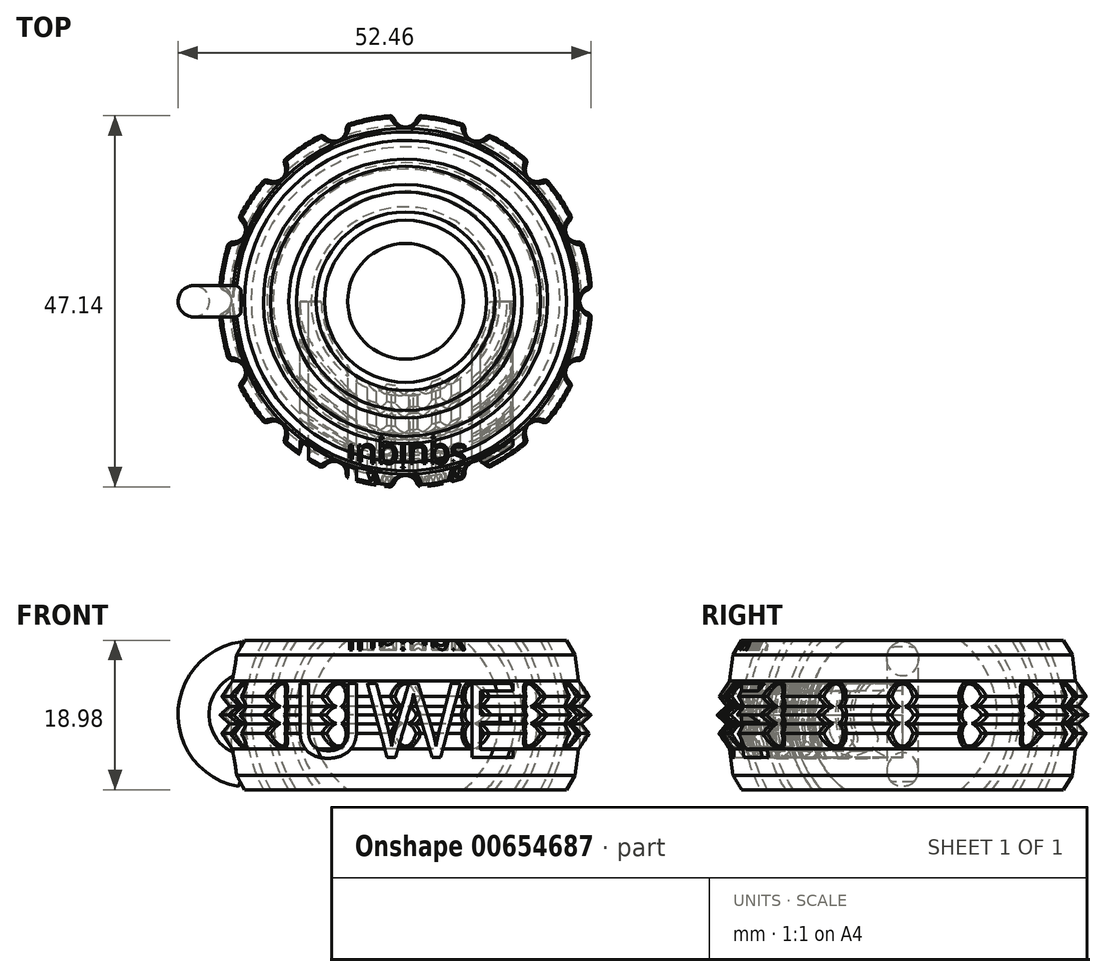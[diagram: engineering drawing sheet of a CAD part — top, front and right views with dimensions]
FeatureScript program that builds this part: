
annotation { "Feature Type Name" : "Feature", "Feature Type Description" : "" }
export const myFeature = defineFeature(function(context is Context, id is Id, definition is map)
    precondition{}
    {
        {
            var Q0;
            Q0=qCreatedBy(makeId("Top.planeOp"),FACE);
            var sketch = newSketch(context, id + "F0", { "sketchPlane" : qUnion([Q0])});
            skArc(sketch, "E0", {"start": v(0, 12) * mm, "mid": v(-12, 0) * mm, "end": v(0, -12) * mm});
            skLineSegment(sketch, "E1", {"start": v(0, 12) * mm, "end": v(0, -12) * mm});
            skArc(sketch, "E2.0", {"start": v(0, 14) * mm, "mid": v(-14, 0) * mm, "end": v(0, -14) * mm});
            skLineSegment(sketch, "E3", {"start": v(0, 14) * mm, "end": v(0, 12) * mm});
            skLineSegment(sketch, "E4", {"start": v(0, -12) * mm, "end": v(0, -14) * mm});
            skSolve(sketch);
        }
        {
            var Q0;
            Q0=makeQuery(id+"F0.imprint","IMPRINT",FACE,{"disambiguationData":[TD([[makeQuery(id+"F0.imprint","IMPRINT",EDGE,{"derivedFrom":sQuery(id+"F0.wireOp",EDGE,"E0")}),-1.0]])]});
            var Q1;
            Q1=sQuery(id+"F0.wireOp",EDGE,"E1");
            revolve(context, id + "F1", {"entities" : qUnion([Q0]), "axis" : qUnion([Q1]), "revolveType" : RevolveType.FULL});
        }
        {
            var Q0;
            Q0=qCreatedBy(makeId("Top.planeOp"),FACE);
            var sketch = newSketch(context, id + "F2", { "sketchPlane" : qUnion([Q0])});
            skLineSegment(sketch, "E5.bottom", {"start": v(37.77, 9.49) * mm, "end": v(-37.77, 9.49) * mm});
            skLineSegment(sketch, "E5.top", {"start": v(37.77, 45.25) * mm, "end": v(-37.77, 45.25) * mm});
            skLineSegment(sketch, "E5.left", {"start": v(37.77, 9.49) * mm, "end": v(37.77, 45.25) * mm});
            skLineSegment(sketch, "E5.right", {"start": v(-37.77, 9.49) * mm, "end": v(-37.77, 45.25) * mm});
            skPoint(sketch, "E5.middle", {"position": v(0, 27.37) * mm});
            skLineSegment(sketch, "E6.MirrorCS", {"start": v(-37.77, -9.49) * mm, "end": v(-37.77, -45.25) * mm});
            skLineSegment(sketch, "E7.MirrorCS", {"start": v(37.77, -9.49) * mm, "end": v(37.77, -45.25) * mm});
            skLineSegment(sketch, "E8.MirrorCS", {"start": v(37.77, -45.25) * mm, "end": v(-37.77, -45.25) * mm});
            skLineSegment(sketch, "E9.MirrorCS", {"start": v(37.77, -9.49) * mm, "end": v(-37.77, -9.49) * mm});
            skPoint(sketch, "E10.MirrorP", {"position": v(0, -27.37) * mm});
            skSolve(sketch);
        }
        {
            var Q0;
            Q0=qCreatedBy(makeId("Top.planeOp"),FACE);
            var sketch = newSketch(context, id + "F3", { "sketchPlane" : qUnion([Q0])});
            skArc(sketch, "E11.0", {"start": v(0, 14.8) * mm, "mid": v(-14.8, 0) * mm, "end": v(0, -14.8) * mm});
            skArc(sketch, "E12.0", {"start": v(0, 16.8) * mm, "mid": v(-16.8, 0) * mm, "end": v(0, -16.8) * mm});
            skLineSegment(sketch, "E13", {"start": v(0, -14.8) * mm, "end": v(0, -16.8) * mm});
            skLineSegment(sketch, "E14", {"start": v(0, 14.8) * mm, "end": v(0, 16.8) * mm});
            skSolve(sketch);
        }
        {
            var Q0;
            Q0=makeQuery(id+"F3.imprint","IMPRINT",FACE,{"disambiguationData":[TD([[makeQuery(id+"F3.imprint","IMPRINT",EDGE,{"derivedFrom":sQuery(id+"F3.wireOp",EDGE,"E11.0")}),-1.0]])]});
            var Q1;
            Q1=sQuery(id+"F0.wireOp",EDGE,"E1");
            revolve(context, id + "F4", {"entities" : qUnion([Q0]), "axis" : qUnion([Q1]), "revolveType" : RevolveType.FULL});
        }
        {
            var Q0;
            Q0=qCreatedBy(makeId("Top.planeOp"),FACE);
            var sketch = newSketch(context, id + "F5", { "sketchPlane" : qUnion([Q0])});
            skArc(sketch, "E15.0", {"start": v(0, 17.6) * mm, "mid": v(-17.6, 0) * mm, "end": v(0, -17.6) * mm});
            skArc(sketch, "E16.0", {"start": v(0, 19.6) * mm, "mid": v(-19.6, 0) * mm, "end": v(0, -19.6) * mm});
            skLineSegment(sketch, "E17", {"start": v(0, -17.6) * mm, "end": v(0, -19.6) * mm});
            skLineSegment(sketch, "E18", {"start": v(0, 17.6) * mm, "end": v(0, 19.6) * mm});
            skSolve(sketch);
        }
        {
            var Q0;
            Q0=qCreatedBy(makeId("Top.planeOp"),FACE);
            var sketch = newSketch(context, id + "F6", { "sketchPlane" : qUnion([Q0])});
            skArc(sketch, "E19.0", {"start": v(0, 20.4) * mm, "mid": v(-20.4, 0) * mm, "end": v(0, -20.4) * mm});
            skArc(sketch, "E20.0", {"start": v(0, 22.4) * mm, "mid": v(-6.34, 21.48) * mm, "end": v(-12.16, 18.81) * mm});
            skLineSegment(sketch, "E21", {"start": v(0, -20.4) * mm, "end": v(0, -22.4) * mm});
            skLineSegment(sketch, "E22", {"start": v(0, 20.4) * mm, "end": v(0, 22.4) * mm});
            skLineSegment(sketch, "E23", {"start": v(-12.16, 18.81) * mm, "end": v(-15.27, 18.35) * mm});
            skLineSegment(sketch, "E24", {"start": v(-15.27, 18.35) * mm, "end": v(-15.27, 16.39) * mm});
            skLineSegment(sketch, "E25", {"start": v(-15.27, 16.39) * mm, "end": v(-19.46, 13.16) * mm});
            skLineSegment(sketch, "E26", {"start": v(-19.46, 13.16) * mm, "end": v(-19.3, 11.37) * mm});
            skLineSegment(sketch, "E27", {"start": v(-19.3, 11.37) * mm, "end": v(-21.55, 7.65) * mm});
            skLineSegment(sketch, "E28", {"start": v(-21.55, 7.65) * mm, "end": v(-21.98, 4.32) * mm});
            skLineSegment(sketch, "E29", {"start": v(-21.98, 4.32) * mm, "end": v(-23.4, 2.34) * mm});
            skLineSegment(sketch, "E30", {"start": v(-23.4, 2.34) * mm, "end": v(-22.37, 1.12) * mm});
            skLineSegment(sketch, "E31", {"start": v(-22.37, 1.12) * mm, "end": v(-23.66, 0) * mm});
            skArc(sketch, "E32.trimOffspring", {"start": v(-12.16, -18.81) * mm, "mid": v(-6.34, -21.48) * mm, "end": v(0, -22.4) * mm});
            skLineSegment(sketch, "E33.MirrorCS", {"start": v(-23.4, -2.34) * mm, "end": v(-22.37, -1.12) * mm});
            skLineSegment(sketch, "E34.MirrorCS", {"start": v(-23.66, 0) * mm, "end": v(-22.4, 0) * mm});
            skLineSegment(sketch, "E35.MirrorCS", {"start": v(-21.98, -4.32) * mm, "end": v(-23.4, -2.34) * mm});
            skLineSegment(sketch, "E36.MirrorCS", {"start": v(-19.46, -13.16) * mm, "end": v(-19.3, -11.37) * mm});
            skLineSegment(sketch, "E37.MirrorCS", {"start": v(-15.27, -18.35) * mm, "end": v(-15.27, -16.39) * mm});
            skLineSegment(sketch, "E38.MirrorCS", {"start": v(-22.37, -1.12) * mm, "end": v(-23.66, 0) * mm});
            skLineSegment(sketch, "E39.MirrorCS", {"start": v(-19.3, -11.37) * mm, "end": v(-21.55, -7.65) * mm});
            skLineSegment(sketch, "E40.MirrorCS", {"start": v(-21.55, -7.65) * mm, "end": v(-21.98, -4.32) * mm});
            skLineSegment(sketch, "E41.MirrorCS", {"start": v(-12.16, -18.81) * mm, "end": v(-15.27, -18.35) * mm});
            skLineSegment(sketch, "E42.MirrorCS", {"start": v(-15.27, -16.39) * mm, "end": v(-19.46, -13.16) * mm});
            skPoint(sketch, "E43.end.orphan", {"position": v(-22.4, 0) * mm});
            skSolve(sketch);
        }
        {
            var Q0;
            Q0=makeQuery(id+"F5.imprint","IMPRINT",FACE,{"disambiguationData":[TD([[makeQuery(id+"F5.imprint","IMPRINT",EDGE,{"derivedFrom":sQuery(id+"F5.wireOp",EDGE,"E15.0")}),-1.0]])]});
            var Q1;
            Q1=sQuery(id+"F0.wireOp",EDGE,"E1");
            revolve(context, id + "F7", {"entities" : qUnion([Q0]), "axis" : qUnion([Q1]), "revolveType" : RevolveType.FULL});
        }
        {
            var Q0;
            Q0=makeQuery(id+"F6.imprint","IMPRINT",FACE,{"disambiguationData":[TD([[makeQuery(id+"F6.imprint","IMPRINT",EDGE,{"derivedFrom":sQuery(id+"F6.wireOp",EDGE,"E19.0")}),-1.0]])]});
            var Q1;
            Q1=sQuery(id+"F0.wireOp",EDGE,"E1");
            revolve(context, id + "F8", {"entities" : qUnion([Q0]), "axis" : qUnion([Q1]), "revolveType" : RevolveType.FULL});
        }
        {
            var Q0;
            Q0 = qSketchRegion(id + "F2", true);
            extrude(context, id + "F9", {"entities" : qUnion([Q0]), "operationType" : NewBodyOperationType.REMOVE, "endBound" : BoundingType.SYMMETRIC, "oppositeDirection" : true, "depth" : 114 * mm, "offsetDistance" : 25 * mm});
        }
        {
            var Q0;
            Q0=qCreatedBy(makeId("Right.planeOp"),FACE);
            cPlane(context, id + "F10", {"entities" : qUnion([Q0]), "cplaneType" : CPlaneType.OFFSET, "offset" : 20.9 * mm, "oppositeDirection" : true, "width" : 150 * mm, "height" : 150 * mm});
        }
        {
            var Q0;
            Q0=qCreatedBy(makeId("Top.planeOp"),FACE);
            var sketch = newSketch(context, id + "F11", { "sketchPlane" : qUnion([Q0])});
            skArc(sketch, "E44", {"start": v(-20.93, 8.53) * mm, "mid": v(-28.13, 0.1) * mm, "end": v(-20.96, -8.37) * mm});
            skSolve(sketch);
        }
        {
            var Q0;
            Q0=qCreatedBy(id+"F10.planeOp",FACE);
            var sketch = newSketch(context, id + "F12", { "sketchPlane" : qUnion([Q0])});
            skCircle(sketch, "E45", {"center": v(7.3, 0) * mm, "radius": 2 * mm});
            skSolve(sketch);
        }
        {
            var Q0;
            Q0=qCreatedBy(makeId("Front.planeOp"),FACE);
            var sketch = newSketch(context, id + "F13", { "sketchPlane" : qUnion([Q0])});
            skCircle(sketch, "E46", {"center": v(23.63, 0) * mm, "radius": 1.5 * mm});
            skCircle(sketch, "E47.1.0", {"center": v(21.83, 9.04) * mm, "radius": 1.5 * mm});
            skCircle(sketch, "E47.2.0", {"center": v(16.7, 16.7) * mm, "radius": 1.5 * mm});
            skCircle(sketch, "E47.3.0", {"center": v(9.04, 21.83) * mm, "radius": 1.5 * mm});
            skCircle(sketch, "E47.4.0", {"center": v(0, 23.63) * mm, "radius": 1.5 * mm});
            skCircle(sketch, "E47.5.0", {"center": v(-9.04, 21.83) * mm, "radius": 1.5 * mm});
            skCircle(sketch, "E47.6.0", {"center": v(-16.7, 16.7) * mm, "radius": 1.5 * mm});
            skCircle(sketch, "E47.7.0", {"center": v(-21.83, 9.04) * mm, "radius": 1.5 * mm});
            skCircle(sketch, "E47.8.0", {"center": v(-23.63, 0) * mm, "radius": 1.5 * mm});
            skCircle(sketch, "E47.9.0", {"center": v(-21.83, -9.04) * mm, "radius": 1.5 * mm});
            skCircle(sketch, "E47.10.0", {"center": v(-16.7, -16.7) * mm, "radius": 1.5 * mm});
            skCircle(sketch, "E47.11.0", {"center": v(-9.04, -21.83) * mm, "radius": 1.5 * mm});
            skCircle(sketch, "E47.12.0", {"center": v(0, -23.63) * mm, "radius": 1.5 * mm});
            skCircle(sketch, "E47.13.0", {"center": v(9.04, -21.83) * mm, "radius": 1.5 * mm});
            skCircle(sketch, "E47.14.0", {"center": v(16.7, -16.7) * mm, "radius": 1.5 * mm});
            skCircle(sketch, "E47.15.0", {"center": v(21.83, -9.04) * mm, "radius": 1.5 * mm});
            skPoint(sketch, "E47.center", {"position": v(0, 0) * mm});
            skSolve(sketch);
        }
        {
            var Q0;
            Q0 = qSketchRegion(id + "F13", true);
            extrude(context, id + "F14", {"entities" : qUnion([Q0]), "operationType" : NewBodyOperationType.REMOVE, "endBound" : BoundingType.SYMMETRIC, "oppositeDirection" : true, "depth" : 25 * mm, "offsetDistance" : 25 * mm});
        }
        {
            var Q0;
            Q0=makeQuery(id+"F12.imprint","IMPRINT",FACE,{"disambiguationData":[TD([[makeQuery(id+"F12.imprint","IMPRINT",EDGE,{"derivedFrom":sQuery(id+"F12.wireOp",EDGE,"E45")}),1.0]])]});
            var Q1;
            Q1=sQuery(id+"F11.wireOp",EDGE,"E44");
            sweep(context, id + "F15", {"operationType" : NewBodyOperationType.ADD, "profiles" : qUnion([Q0]), "path" : qUnion([Q1])});
        }
        {
            var Q0;
            Q0=makeQuery(id+"F14.boolean.opBoolean","COPY",FACE,{"derivedFrom":makeQuery(id+"F14.opExtrude","SWEPT_FACE",FACE,{"disambiguationData":[OSD([sQuery(id+"F13.wireOp",EDGE,"E46")])]})});
            var Q1;
            Q1=makeQuery(id+"F14.boolean.opBoolean","COPY",FACE,{"derivedFrom":makeQuery(id+"F14.opExtrude","SWEPT_FACE",FACE,{"disambiguationData":[OSD([sQuery(id+"F13.wireOp",EDGE,"E47.1.0")])]})});
            var Q2;
            Q2=makeQuery(id+"F14.boolean.opBoolean","COPY",FACE,{"derivedFrom":makeQuery(id+"F14.opExtrude","SWEPT_FACE",FACE,{"disambiguationData":[OSD([sQuery(id+"F13.wireOp",EDGE,"E47.2.0")])]})});
            var Q3;
            Q3=makeQuery(id+"F14.boolean.opBoolean","COPY",FACE,{"derivedFrom":makeQuery(id+"F14.opExtrude","SWEPT_FACE",FACE,{"disambiguationData":[OSD([sQuery(id+"F13.wireOp",EDGE,"E47.15.0")])]})});
            var Q4;
            Q4=makeQuery(id+"F14.boolean.opBoolean","COPY",FACE,{"derivedFrom":makeQuery(id+"F14.opExtrude","SWEPT_FACE",FACE,{"disambiguationData":[OSD([sQuery(id+"F13.wireOp",EDGE,"E47.14.0")])]})});
            var Q5;
            Q5=makeQuery(id+"F14.boolean.opBoolean","COPY",FACE,{"derivedFrom":makeQuery(id+"F14.opExtrude","SWEPT_FACE",FACE,{"disambiguationData":[OSD([sQuery(id+"F13.wireOp",EDGE,"E47.13.0")])]})});
            var Q6;
            Q6=makeQuery(id+"F14.boolean.opBoolean","COPY",FACE,{"derivedFrom":makeQuery(id+"F14.opExtrude","SWEPT_FACE",FACE,{"disambiguationData":[OSD([sQuery(id+"F13.wireOp",EDGE,"E47.12.0")])]})});
            var Q7;
            Q7=makeQuery(id+"F14.boolean.opBoolean","INTERSECT",EDGE,{"disambiguationData":[OD(0.0)],"derivedFrom":[makeQuery(id+"F8.opRevolve","SWEPT_FACE",FACE,{"disambiguationData":[OSD([sQuery(id+"F6.wireOp",EDGE,"E38.MirrorCS")])]}),makeQuery(id+"F14.opExtrude","SWEPT_FACE",FACE,{"disambiguationData":[OSD([sQuery(id+"F13.wireOp",EDGE,"E47.11.0")])]})]});
            var Q8;
            Q8=makeQuery(id+"F14.boolean.opBoolean","COPY",FACE,{"derivedFrom":makeQuery(id+"F14.opExtrude","SWEPT_FACE",FACE,{"disambiguationData":[OSD([sQuery(id+"F13.wireOp",EDGE,"E47.11.0")])]})});
            var Q9;
            Q9=makeQuery(id+"F14.boolean.opBoolean","COPY",FACE,{"derivedFrom":makeQuery(id+"F14.opExtrude","SWEPT_FACE",FACE,{"disambiguationData":[OSD([sQuery(id+"F13.wireOp",EDGE,"E47.10.0")])]})});
            var Q10;
            Q10=makeQuery(id+"F14.boolean.opBoolean","COPY",FACE,{"derivedFrom":makeQuery(id+"F14.opExtrude","SWEPT_FACE",FACE,{"disambiguationData":[OSD([sQuery(id+"F13.wireOp",EDGE,"E47.9.0")])]})});
            var Q11;
            Q11=makeQuery(id+"F14.boolean.opBoolean","COPY",FACE,{"disambiguationData":[TD([makeQuery(id+"F8.opRevolve","SWEPT_FACE",FACE,{"disambiguationData":[OSD([sQuery(id+"F6.wireOp",EDGE,"E29")])]})])],"derivedFrom":makeQuery(id+"F14.opExtrude","SWEPT_FACE",FACE,{"disambiguationData":[OSD([sQuery(id+"F13.wireOp",EDGE,"E47.8.0")])]})});
            var Q12;
            Q12=makeQuery(id+"F14.boolean.opBoolean","COPY",FACE,{"derivedFrom":makeQuery(id+"F14.opExtrude","SWEPT_FACE",FACE,{"disambiguationData":[OSD([sQuery(id+"F13.wireOp",EDGE,"E47.7.0")])]})});
            var Q13;
            Q13=makeQuery(id+"F14.boolean.opBoolean","COPY",FACE,{"derivedFrom":makeQuery(id+"F14.opExtrude","SWEPT_FACE",FACE,{"disambiguationData":[OSD([sQuery(id+"F13.wireOp",EDGE,"E47.6.0")])]})});
            var Q14;
            Q14=makeQuery(id+"F14.boolean.opBoolean","COPY",FACE,{"derivedFrom":makeQuery(id+"F14.opExtrude","SWEPT_FACE",FACE,{"disambiguationData":[OSD([sQuery(id+"F13.wireOp",EDGE,"E47.5.0")])]})});
            var Q15;
            Q15=makeQuery(id+"F14.boolean.opBoolean","COPY",FACE,{"derivedFrom":makeQuery(id+"F14.opExtrude","SWEPT_FACE",FACE,{"disambiguationData":[OSD([sQuery(id+"F13.wireOp",EDGE,"E47.4.0")])]})});
            var Q16;
            Q16=makeQuery(id+"F14.boolean.opBoolean","COPY",FACE,{"derivedFrom":makeQuery(id+"F14.opExtrude","SWEPT_FACE",FACE,{"disambiguationData":[OSD([sQuery(id+"F13.wireOp",EDGE,"E47.3.0")])]})});
            fillet(context, id + "F16", {"entities" : qUnion([Q0, Q1, Q2, Q3, Q4, Q5, Q6, Q7, Q8, Q9, Q10, Q11, Q12, Q13, Q14, Q15, Q16]), "radius" : 0.5 * mm, "tangentPropagation" : true, "allowEdgeOverflow" : false});
        }
        {
            var Q0;
            Q0=makeQuery(id+"F9.boolean.opBoolean","COPY",FACE,{"disambiguationData":[TD([makeQuery(id+"F1.opRevolve","SWEPT_FACE",FACE,{"disambiguationData":[OSD([sQuery(id+"F0.wireOp",EDGE,"E0")])]})])],"derivedFrom":makeQuery(id+"F9.opExtrude","SWEPT_FACE",FACE,{"disambiguationData":[OSD([sQuery(id+"F2.wireOp",EDGE,"E5.bottom")])]})});
            var sketch = newSketch(context, id + "F17", { "sketchPlane" : qUnion([Q0])});
            skText(sketch, "E48", { "text": "squiqui", "fontName": "OpenSans-Regular.ttf"});
            const initialGuessF17  = {"E48": [-0.0078, 0.01824, 1, 0, 0.0032]};
            skSetInitialGuess(sketch, initialGuessF17);
            skSolve(sketch);
        }
        {
            var Q0;
            Q0 = qSketchRegion(id + "F17", true);
            extrude(context, id + "F18", {"entities" : qUnion([Q0]), "operationType" : NewBodyOperationType.REMOVE, "oppositeDirection" : true, "depth" : 1.2 * mm, "offsetDistance" : 25 * mm});
        }
        {
            var Q0;
            Q0=qCreatedBy(makeId("Top.planeOp"),FACE);
            var sketch = newSketch(context, id + "F19", { "sketchPlane" : qUnion([Q0])});
            skLineSegment(sketch, "E49", {"start": v(33.61, 0) * mm, "end": v(-41.39, 0) * mm});
            skSolve(sketch);
        }
        {
            var Q0;
            Q0=makeQuery(id+"F1.opRevolve","SWEPT_BODY",BODY,{"disambiguationData":[OSD([sQuery(id+"F0.wireOp",EDGE,"E0"),sQuery(id+"F0.wireOp",EDGE,"E2.0"),sQuery(id+"F0.wireOp",EDGE,"E3"),sQuery(id+"F0.wireOp",EDGE,"E4")])]});
            var Q1;
            Q1=makeQuery(id+"F4.opRevolve","SWEPT_BODY",BODY,{"disambiguationData":[OSD([sQuery(id+"F3.wireOp",EDGE,"E11.0"),sQuery(id+"F3.wireOp",EDGE,"E12.0"),sQuery(id+"F3.wireOp",EDGE,"E13"),sQuery(id+"F3.wireOp",EDGE,"E14")])]});
            var Q2;
            Q2=makeQuery(id+"F8.opRevolve","SWEPT_BODY",BODY,{"disambiguationData":[OSD([sQuery(id+"F6.wireOp",EDGE,"E19.0"),sQuery(id+"F6.wireOp",EDGE,"E20.0"),sQuery(id+"F6.wireOp",EDGE,"E21"),sQuery(id+"F6.wireOp",EDGE,"E22"),sQuery(id+"F6.wireOp",EDGE,"E23"),sQuery(id+"F6.wireOp",EDGE,"E24"),sQuery(id+"F6.wireOp",EDGE,"E25"),sQuery(id+"F6.wireOp",EDGE,"E26"),sQuery(id+"F6.wireOp",EDGE,"E27"),sQuery(id+"F6.wireOp",EDGE,"E28"),sQuery(id+"F6.wireOp",EDGE,"E29"),sQuery(id+"F6.wireOp",EDGE,"E30"),sQuery(id+"F6.wireOp",EDGE,"E31"),sQuery(id+"F6.wireOp",EDGE,"E32.trimOffspring"),sQuery(id+"F6.wireOp",EDGE,"E33.MirrorCS"),sQuery(id+"F6.wireOp",EDGE,"E35.MirrorCS"),sQuery(id+"F6.wireOp",EDGE,"E36.MirrorCS"),sQuery(id+"F6.wireOp",EDGE,"E37.MirrorCS"),sQuery(id+"F6.wireOp",EDGE,"E38.MirrorCS"),sQuery(id+"F6.wireOp",EDGE,"E39.MirrorCS"),sQuery(id+"F6.wireOp",EDGE,"E40.MirrorCS"),sQuery(id+"F6.wireOp",EDGE,"E41.MirrorCS"),sQuery(id+"F6.wireOp",EDGE,"E42.MirrorCS")])]});
            var Q3;
            Q3=makeQuery(id+"F7.opRevolve","SWEPT_BODY",BODY,{"disambiguationData":[OSD([sQuery(id+"F5.wireOp",EDGE,"E15.0"),sQuery(id+"F5.wireOp",EDGE,"E16.0"),sQuery(id+"F5.wireOp",EDGE,"E17"),sQuery(id+"F5.wireOp",EDGE,"E18")])]});
            var Q4;
            Q4=sQuery(id+"F19.wireOp",EDGE,"E49");
            transform(context, id + "F20", {"entities" : qUnion([Q0, Q1, Q2, Q3]), "transformType" : TransformType.ROTATION, "transformAxis" : qUnion([Q4]), "angle" : 90 * degree, "oppositeDirection" : true, "makeCopy" : false});
        }
        {
            var Q0;
            Q0=qCreatedBy(makeId("Front.planeOp"),FACE);
            var sketch = newSketch(context, id + "F21", { "sketchPlane" : qUnion([Q0])});
            skText(sketch, "E50", { "text": "UWE", "fontName": "OpenSans-Regular.ttf"});
            const initialGuessF21  = {"E50": [-0.0146, -0.00536, 1, 0, 0.00947]};
            skSetInitialGuess(sketch, initialGuessF21);
            skSolve(sketch);
        }
        {
            var Q0;
            Q0 = qSketchRegion(id + "F21", true);
            extrude(context, id + "F22", {"entities" : qUnion([Q0]), "operationType" : NewBodyOperationType.REMOVE, "depth" : 25 * mm, "offsetDistance" : 25 * mm});
        }
    });
